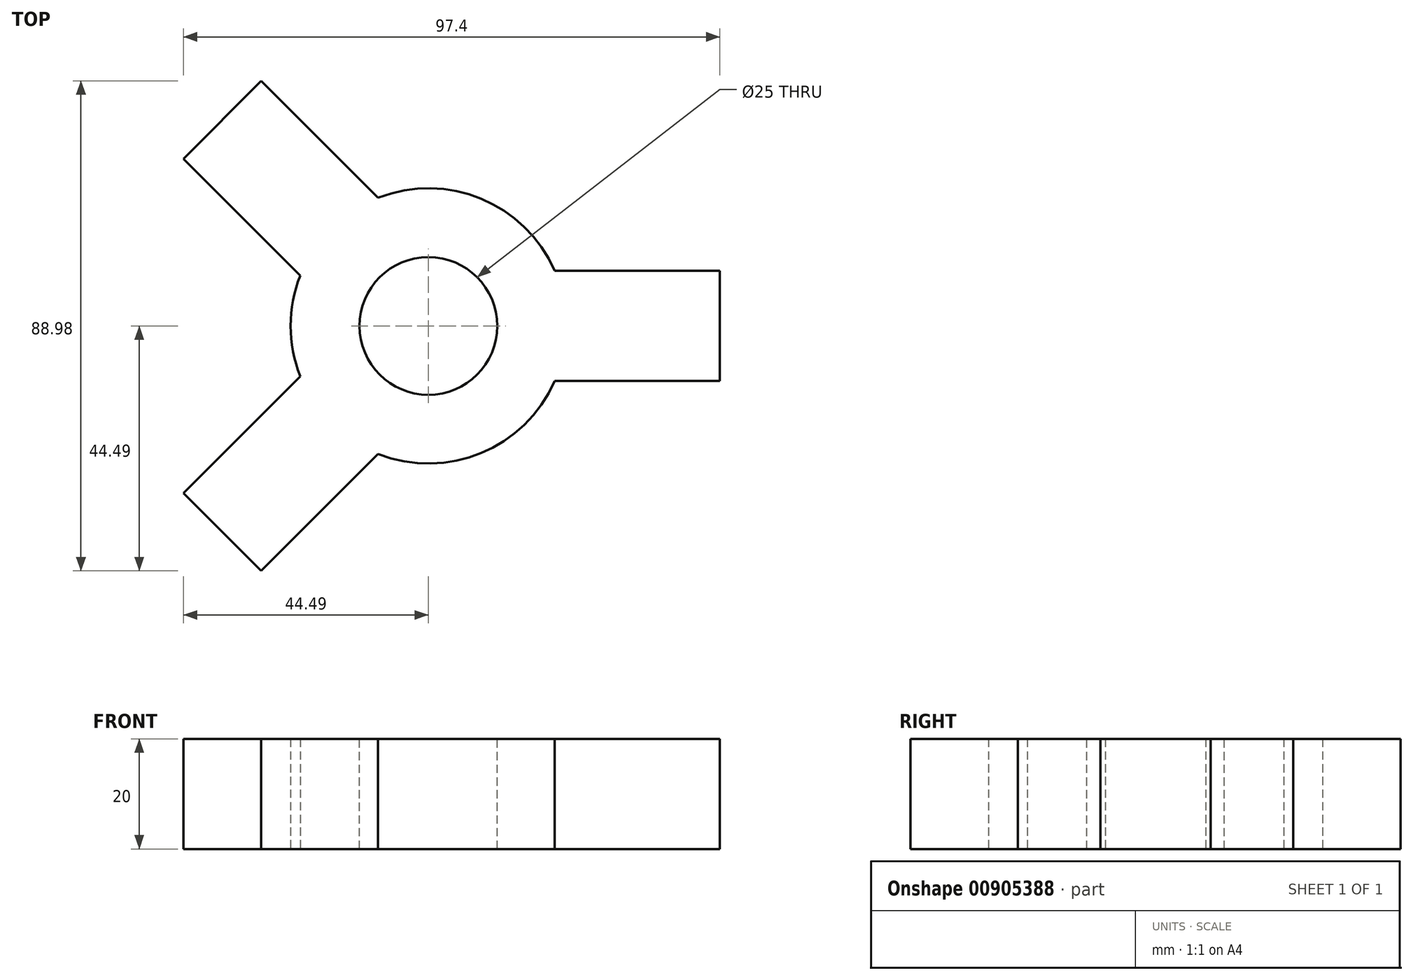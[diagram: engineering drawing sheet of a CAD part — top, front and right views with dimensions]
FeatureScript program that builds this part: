
annotation { "Feature Type Name" : "Feature", "Feature Type Description" : "" }
export const myFeature = defineFeature(function(context is Context, id is Id, definition is map)
    precondition{}
    {
        {
            assignVariable(context, id + "F0", {"name" : "Dicke", "anyValue" : 20});
        }
        {
            var Q0;
            Q0=qCreatedBy(makeId("Top.planeOp"),FACE);
            var sketch = newSketch(context, id + "F1", { "sketchPlane" : qUnion([Q0])});
            skCircle(sketch, "E0", {"center": v(0, 0) * mm, "radius": 25 * mm});
            skLineSegment(sketch, "E1", {"start": v(22.91, 0) * mm, "end": v(22.91, 10) * mm});
            skLineSegment(sketch, "E2", {"start": v(22.91, 10) * mm, "end": v(52.91, 10) * mm});
            skLineSegment(sketch, "E3", {"start": v(52.91, 10) * mm, "end": v(52.91, -10) * mm});
            skLineSegment(sketch, "E4", {"start": v(52.91, -10) * mm, "end": v(22.91, -10) * mm});
            skLineSegment(sketch, "E5", {"start": v(22.91, -10) * mm, "end": v(22.91, 0) * mm});
            skLineSegment(sketch, "E6", {"start": v(-37.42, 37.42) * mm, "end": v(0, 0) * mm, "construction": true});
            skLineSegment(sketch, "E7", {"start": v(0, 0) * mm, "end": v(-27.44, -27.44) * mm, "construction": true});
            skLineSegment(sketch, "E8", {"start": v(-37.42, 37.42) * mm, "end": v(-30.34, 44.49) * mm});
            skLineSegment(sketch, "E9", {"start": v(-37.42, 37.42) * mm, "end": v(-44.49, 30.34) * mm});
            skLineSegment(sketch, "E10", {"start": v(-30.34, 44.49) * mm, "end": v(-9.13, 23.27) * mm});
            skLineSegment(sketch, "E11", {"start": v(-9.13, 23.27) * mm, "end": v(-23.27, 9.13) * mm});
            skLineSegment(sketch, "E12", {"start": v(-44.49, 30.34) * mm, "end": v(-23.27, 9.13) * mm});
            skLineSegment(sketch, "E13.MirrorCS", {"start": v(-44.49, -30.34) * mm, "end": v(-23.27, -9.13) * mm});
            skLineSegment(sketch, "E14.MirrorCS", {"start": v(-37.42, -37.42) * mm, "end": v(-30.34, -44.49) * mm});
            skLineSegment(sketch, "E15.MirrorCS", {"start": v(-37.42, -37.42) * mm, "end": v(-44.49, -30.34) * mm});
            skLineSegment(sketch, "E16.MirrorCS", {"start": v(-30.34, -44.49) * mm, "end": v(-9.13, -23.27) * mm});
            skLineSegment(sketch, "E17.MirrorCS", {"start": v(-9.13, -23.27) * mm, "end": v(-23.27, -9.13) * mm});
            skSolve(sketch);
        }
        {
            var Q0;
            Q0 = qSketchRegion(id + "F1", true);
            extrude(context, id + "F2", {"entities" : qUnion([Q0]), "depth" : getVariable(context, 'Dicke') * mm, "offsetDistance" : 25 * mm});
        }
        {
            var Q0;
            Q0=makeQuery(id+"F2.opExtrude","CAP_FACE",FACE,{"disambiguationData":[OSD([sQuery(id+"F1.wireOp",EDGE,"E0"),sQuery(id+"F1.wireOp",EDGE,"E2"),sQuery(id+"F1.wireOp",EDGE,"E3"),sQuery(id+"F1.wireOp",EDGE,"E4"),sQuery(id+"F1.wireOp",EDGE,"E8"),sQuery(id+"F1.wireOp",EDGE,"E9"),sQuery(id+"F1.wireOp",EDGE,"E10"),sQuery(id+"F1.wireOp",EDGE,"E12"),sQuery(id+"F1.wireOp",EDGE,"E13.MirrorCS"),sQuery(id+"F1.wireOp",EDGE,"E14.MirrorCS"),sQuery(id+"F1.wireOp",EDGE,"E15.MirrorCS"),sQuery(id+"F1.wireOp",EDGE,"E16.MirrorCS")])],"isStart":false});
            var sketch = newSketch(context, id + "F3", { "sketchPlane" : qUnion([Q0])});
            skCircle(sketch, "E18", {"center": v(0, 0) * mm, "radius": 12.5 * mm});
            skSolve(sketch);
        }
        {
            var Q0;
            Q0=makeQuery(id+"F3.imprint","IMPRINT",FACE,{"disambiguationData":[TD([[makeQuery(id+"F3.imprint","IMPRINT",EDGE,{"derivedFrom":sQuery(id+"F3.wireOp",EDGE,"E18")}),1.0]])]});
            extrude(context, id + "F4", {"entities" : qUnion([Q0]), "operationType" : NewBodyOperationType.REMOVE, "oppositeDirection" : true, "depth" : 25 * mm, "offsetDistance" : 25 * mm});
        }
    });
